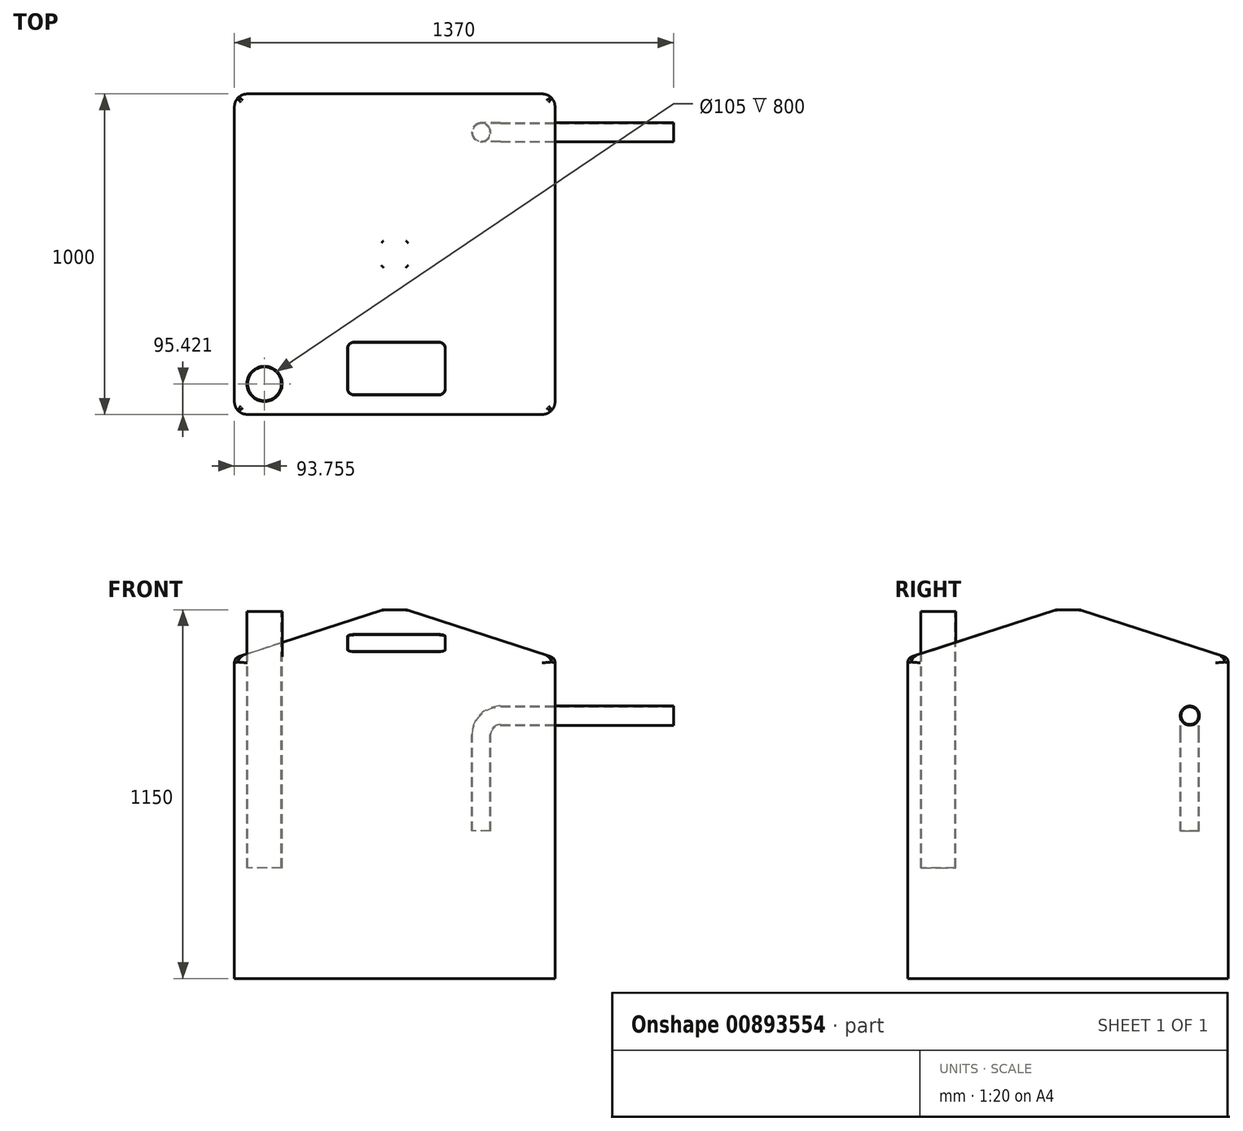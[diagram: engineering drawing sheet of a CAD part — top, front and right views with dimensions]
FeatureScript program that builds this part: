
annotation { "Feature Type Name" : "Feature", "Feature Type Description" : "" }
export const myFeature = defineFeature(function(context is Context, id is Id, definition is map)
    precondition{}
    {
        {
            var Q0;
            Q0=qCreatedBy(makeId("Top.planeOp"),FACE);
            var sketch = newSketch(context, id + "F0", { "sketchPlane" : qUnion([Q0])});
            skLineSegment(sketch, "E0.bottom", {"start": v(-500, 500) * mm, "end": v(500, 500) * mm});
            skLineSegment(sketch, "E0.top", {"start": v(-500, -500) * mm, "end": v(500, -500) * mm});
            skLineSegment(sketch, "E0.left", {"start": v(-500, 500) * mm, "end": v(-500, -500) * mm});
            skLineSegment(sketch, "E0.right", {"start": v(500, 500) * mm, "end": v(500, -500) * mm});
            skPoint(sketch, "E0.middle", {"position": v(0, 0) * mm});
            skSolve(sketch);
        }
        {
            var Q0;
            Q0=makeQuery(id+"F0.imprint","IMPRINT",FACE,{"disambiguationData":[TD([[makeQuery(id+"F0.imprint","IMPRINT",EDGE,{"derivedFrom":sQuery(id+"F0.wireOp",EDGE,"E0.bottom")}),-1.0]])]});
            extrude(context, id + "F1", {"entities" : qUnion([Q0]), "depth" : 1000 * mm, "offsetDistance" : 25 * mm});
        }
        {
            var Q0;
            Q0=makeQuery(id+"F1.opExtrude","CAP_FACE",FACE,{"disambiguationData":[OSD([sQuery(id+"F0.wireOp",EDGE,"E0.bottom"),sQuery(id+"F0.wireOp",EDGE,"E0.top"),sQuery(id+"F0.wireOp",EDGE,"E0.left"),sQuery(id+"F0.wireOp",EDGE,"E0.right")])],"isStart":false});
            var sketch = newSketch(context, id + "F2", { "sketchPlane" : qUnion([Q0])});
            skLineSegment(sketch, "E1.bottom", {"start": v(-500, 500) * mm, "end": v(500, 500) * mm});
            skLineSegment(sketch, "E1.top", {"start": v(-500, -500) * mm, "end": v(500, -500) * mm});
            skLineSegment(sketch, "E1.left", {"start": v(-500, 500) * mm, "end": v(-500, -500) * mm});
            skLineSegment(sketch, "E1.right", {"start": v(500, 500) * mm, "end": v(500, -500) * mm});
            skSolve(sketch);
        }
        {
            var Q0;
            Q0 = qSketchRegion(id + "F2", true);
            extrude(context, id + "F3", {"entities" : qUnion([Q0]), "operationType" : NewBodyOperationType.ADD, "depth" : 150 * mm, "offsetDistance" : 25 * mm, "hasDraft" : true, "draftAngle" : 72 * degree, "draftPullDirection" : true});
        }
        {
            var Q0;
            Q0=makeQuery(id+"F3.opExtrude","CAP_FACE",FACE,{"disambiguationData":[OSD([sQuery(id+"F2.wireOp",EDGE,"E1.bottom"),sQuery(id+"F2.wireOp",EDGE,"E1.top"),sQuery(id+"F2.wireOp",EDGE,"E1.left"),sQuery(id+"F2.wireOp",EDGE,"E1.right")])],"isStart":false});
            cPlane(context, id + "F4", {"entities" : qUnion([Q0]), "cplaneType" : CPlaneType.OFFSET, "offset" : 5 * mm, "oppositeDirection" : true, "width" : 150 * mm, "height" : 150 * mm});
        }
        {
            var Q0;
            Q0=qCreatedBy(id+"F4.planeOp",FACE);
            var sketch = newSketch(context, id + "F5", { "sketchPlane" : qUnion([Q0])});
            skCircle(sketch, "E2", {"center": v(-406.25, -404.58) * mm, "radius": 55 * mm});
            skSolve(sketch);
        }
        {
            var Q0;
            Q0=makeQuery(id+"F1.opExtrude","SWEPT_EDGE",EDGE,{"disambiguationData":[OSD([sQuery(id+"F0.wireOp",EDGE,"E0.bottom"),sQuery(id+"F0.wireOp",EDGE,"E0.right")])]});
            var Q1;
            Q1=makeQuery(id+"F1.opExtrude","SWEPT_EDGE",EDGE,{"disambiguationData":[OSD([sQuery(id+"F0.wireOp",EDGE,"E0.top"),sQuery(id+"F0.wireOp",EDGE,"E0.right")])]});
            var Q2;
            Q2=makeQuery(id+"F1.opExtrude","SWEPT_EDGE",EDGE,{"disambiguationData":[OSD([sQuery(id+"F0.wireOp",EDGE,"E0.top"),sQuery(id+"F0.wireOp",EDGE,"E0.left")])]});
            var Q3;
            Q3=makeQuery(id+"F1.opExtrude","SWEPT_EDGE",EDGE,{"disambiguationData":[OSD([sQuery(id+"F0.wireOp",EDGE,"E0.bottom"),sQuery(id+"F0.wireOp",EDGE,"E0.left")])]});
            fillet(context, id + "F6", {"entities" : qUnion([Q0, Q1, Q2, Q3]), "radius" : 40 * mm, "tangentPropagation" : true, "allowEdgeOverflow" : false});
        }
        {
            var Q0;
            Q0=makeQuery(id+"F3.opExtrude","SWEPT_FACE",FACE,{"disambiguationData":[OSD([sQuery(id+"F2.wireOp",EDGE,"E1.top")])]});
            var Q1;
            Q1=makeQuery(id+"F3.opExtrude","SWEPT_FACE",FACE,{"disambiguationData":[OSD([sQuery(id+"F2.wireOp",EDGE,"E1.right")])]});
            var Q2;
            Q2=makeQuery(id+"F3.opExtrude","SWEPT_FACE",FACE,{"disambiguationData":[OSD([sQuery(id+"F2.wireOp",EDGE,"E1.bottom")])]});
            var Q3;
            Q3=makeQuery(id+"F3.opExtrude","SWEPT_FACE",FACE,{"disambiguationData":[OSD([sQuery(id+"F2.wireOp",EDGE,"E1.left")])]});
            fillet(context, id + "F7", {"entities" : qUnion([Q0, Q1, Q2, Q3]), "radius" : 20 * mm, "tangentPropagation" : true, "allowEdgeOverflow" : false});
        }
        {
            var Q0;
            Q0=makeQuery(id+"F3.opExtrude","SWEPT_FACE",FACE,{"disambiguationData":[OSD([sQuery(id+"F2.wireOp",EDGE,"E1.top")])]});
            var sketch = newSketch(context, id + "F8", { "sketchPlane" : qUnion([Q0])});
            skLineSegment(sketch, "E3.bottom", {"start": v(-127.24, 70.68) * mm, "end": v(137.92, 70.68) * mm});
            skLineSegment(sketch, "E3.top", {"start": v(-127.24, -102.8) * mm, "end": v(137.92, -102.8) * mm});
            skLineSegment(sketch, "E3.left", {"start": v(-147.24, 50.68) * mm, "end": v(-147.24, -82.8) * mm});
            skLineSegment(sketch, "E3.right", {"start": v(157.92, 50.68) * mm, "end": v(157.92, -82.8) * mm});
            skPoint(sketch, "E4.visualSharp", {"position": v(-147.24, 70.68) * mm});
            skArc(sketch, "E4.filletArc", {"start": v(-127.24, 70.68) * mm, "mid": v(-141.38, 64.83) * mm, "end": v(-147.24, 50.68) * mm});
            skPoint(sketch, "E5.visualSharp", {"position": v(157.92, 70.68) * mm});
            skArc(sketch, "E5.filletArc", {"start": v(157.92, 50.68) * mm, "mid": v(152.06, 64.83) * mm, "end": v(137.92, 70.68) * mm});
            skPoint(sketch, "E6.visualSharp", {"position": v(157.92, -102.8) * mm});
            skArc(sketch, "E6.filletArc", {"start": v(137.92, -102.8) * mm, "mid": v(152.06, -96.94) * mm, "end": v(157.92, -82.8) * mm});
            skPoint(sketch, "E7.visualSharp", {"position": v(-147.24, -102.8) * mm});
            skArc(sketch, "E7.filletArc", {"start": v(-147.24, -82.8) * mm, "mid": v(-141.38, -96.94) * mm, "end": v(-127.24, -102.8) * mm});
            skSolve(sketch);
        }
        {
            var Q0;
            Q0=makeQuery(id+"F8.imprint","IMPRINT",FACE,{"disambiguationData":[TD([[makeQuery(id+"F8.imprint","IMPRINT",EDGE,{"derivedFrom":sQuery(id+"F8.wireOp",EDGE,"E3.bottom")}),-1.0]])]});
            extrude(context, id + "F9", {"entities" : qUnion([Q0]), "operationType" : NewBodyOperationType.ADD, "depth" : 0.2 * mm, "offsetDistance" : 25 * mm});
        }
        {
            var Q0;
            Q0=makeQuery(id+"F9.opExtrude","CAP_FACE",FACE,{"disambiguationData":[OSD([sQuery(id+"F8.wireOp",EDGE,"E3.bottom"),sQuery(id+"F8.wireOp",EDGE,"E3.top"),sQuery(id+"F8.wireOp",EDGE,"E3.left"),sQuery(id+"F8.wireOp",EDGE,"E3.right")])],"isStart":false});
            shell(context, id + "F10", {"entities" : qUnion([Q0]), "thickness" : 1 * mm});
        }
        {
            var Q0;
            Q0=makeQuery(id+"F5.imprint","IMPRINT",FACE,{"disambiguationData":[TD([[makeQuery(id+"F5.imprint","IMPRINT",EDGE,{"derivedFrom":sQuery(id+"F5.wireOp",EDGE,"E2")}),1.0]])]});
            var Q1;
            Q1=sQuery(id+"F5.wireOp",EDGE,"E2");
            extrude(context, id + "F11", {"entities" : qUnion([Q0]), "surfaceEntities" : qUnion([Q1]), "oppositeDirection" : true, "depth" : 800 * mm, "offsetDistance" : 25 * mm});
        }
        {
            var Q0;
            Q0=makeQuery(id+"F11.opExtrude","CAP_FACE",FACE,{"disambiguationData":[OSD([sQuery(id+"F5.wireOp",EDGE,"E2")])],"isStart":false});
            var Q1;
            Q1=makeQuery(id+"F11.opExtrude","CAP_FACE",FACE,{"disambiguationData":[OSD([sQuery(id+"F5.wireOp",EDGE,"E2")])],"isStart":true});
            shell(context, id + "F12", {"entities" : qUnion([Q0, Q1]), "thickness" : 2.5 * mm});
        }
        {
            var Q0;
            Q0=makeQuery(id+"F1.opExtrude","SWEPT_FACE",FACE,{"disambiguationData":[OSD([sQuery(id+"F0.wireOp",EDGE,"E0.right")])]});
            var sketch = newSketch(context, id + "F13", { "sketchPlane" : qUnion([Q0])});
            skCircle(sketch, "E8", {"center": v(380, 820) * mm, "radius": 30 * mm});
            skSolve(sketch);
        }
        {
            var Q0;
            Q0=qCreatedBy(makeId("Right.planeOp"),FACE);
            cPlane(context, id + "F14", {"entities" : qUnion([Q0]), "cplaneType" : CPlaneType.OFFSET, "offset" : 820 * mm, "width" : 150 * mm, "height" : 150 * mm});
        }
        {
            var Q0;
            Q0=qCreatedBy(makeId("Front.planeOp"),FACE);
            cPlane(context, id + "F15", {"entities" : qUnion([Q0]), "cplaneType" : CPlaneType.OFFSET, "offset" : 380 * mm, "oppositeDirection" : true, "width" : 150 * mm, "height" : 150 * mm});
        }
        {
            var Q0;
            Q0=makeQuery(id+"F13.imprint","IMPRINT",FACE,{"disambiguationData":[TD([[makeQuery(id+"F13.imprint","IMPRINT",EDGE,{"derivedFrom":sQuery(id+"F13.wireOp",EDGE,"E8")}),1.0]])]});
            extrude(context, id + "F16", {"entities" : qUnion([Q0]), "operationType" : NewBodyOperationType.REMOVE, "oppositeDirection" : true, "depth" : 25 * mm, "offsetDistance" : 25 * mm});
        }
        {
            var Q0;
            Q0=qCreatedBy(id+"F15.planeOp",FACE);
            var sketch = newSketch(context, id + "F17", { "sketchPlane" : qUnion([Q0])});
            skLineSegment(sketch, "E9", {"start": v(870, 820) * mm, "end": v(330, 820) * mm});
            skLineSegment(sketch, "E10", {"start": v(270, 760) * mm, "end": v(270, 460) * mm});
            skPoint(sketch, "E11.visualSharp", {"position": v(270, 820) * mm});
            skArc(sketch, "E11.filletArc", {"start": v(330, 820) * mm, "mid": v(287.57, 802.43) * mm, "end": v(270, 760) * mm});
            skSolve(sketch);
        }
        {
            var Q0;
            Q0=qCreatedBy(id+"F14.planeOp",FACE);
            var sketch = newSketch(context, id + "F18", { "sketchPlane" : qUnion([Q0])});
            skCircle(sketch, "E12", {"center": v(380, 820) * mm, "radius": 30 * mm});
            skSolve(sketch);
        }
        {
            var Q0;
            Q0=makeQuery(id+"F18.imprint","IMPRINT",FACE,{"disambiguationData":[TD([[makeQuery(id+"F18.imprint","IMPRINT",EDGE,{"derivedFrom":sQuery(id+"F18.wireOp",EDGE,"E12")}),1.0]])]});
            var Q1;
            Q1=sQuery(id+"F17.wireOp",EDGE,"E9");
            var Q2;
            Q2=sQuery(id+"F17.wireOp",EDGE,"E11.filletArc");
            var Q3;
            Q3=sQuery(id+"F17.wireOp",EDGE,"E10");
            sweep(context, id + "F19", {"profiles" : qUnion([Q0]), "path" : qUnion([Q1, Q2, Q3])});
        }
        {
            var Q0;
            Q0=makeQuery(id+"F19.opSweep","CAP_FACE",FACE,{"disambiguationData":[OSD([sQuery(id+"F17.wireOp",VERTEX,"E9.start"),sQuery(id+"F18.wireOp",EDGE,"E12")])],"isStart":false});
            var Q1;
            Q1=makeQuery(id+"F19.opSweep","CAP_FACE",FACE,{"disambiguationData":[OSD([sQuery(id+"F17.wireOp",VERTEX,"E10.end"),sQuery(id+"F18.wireOp",EDGE,"E12")])],"isStart":true});
            shell(context, id + "F20", {"entities" : qUnion([Q0, Q1]), "thickness" : 2.5 * mm});
        }
    });
